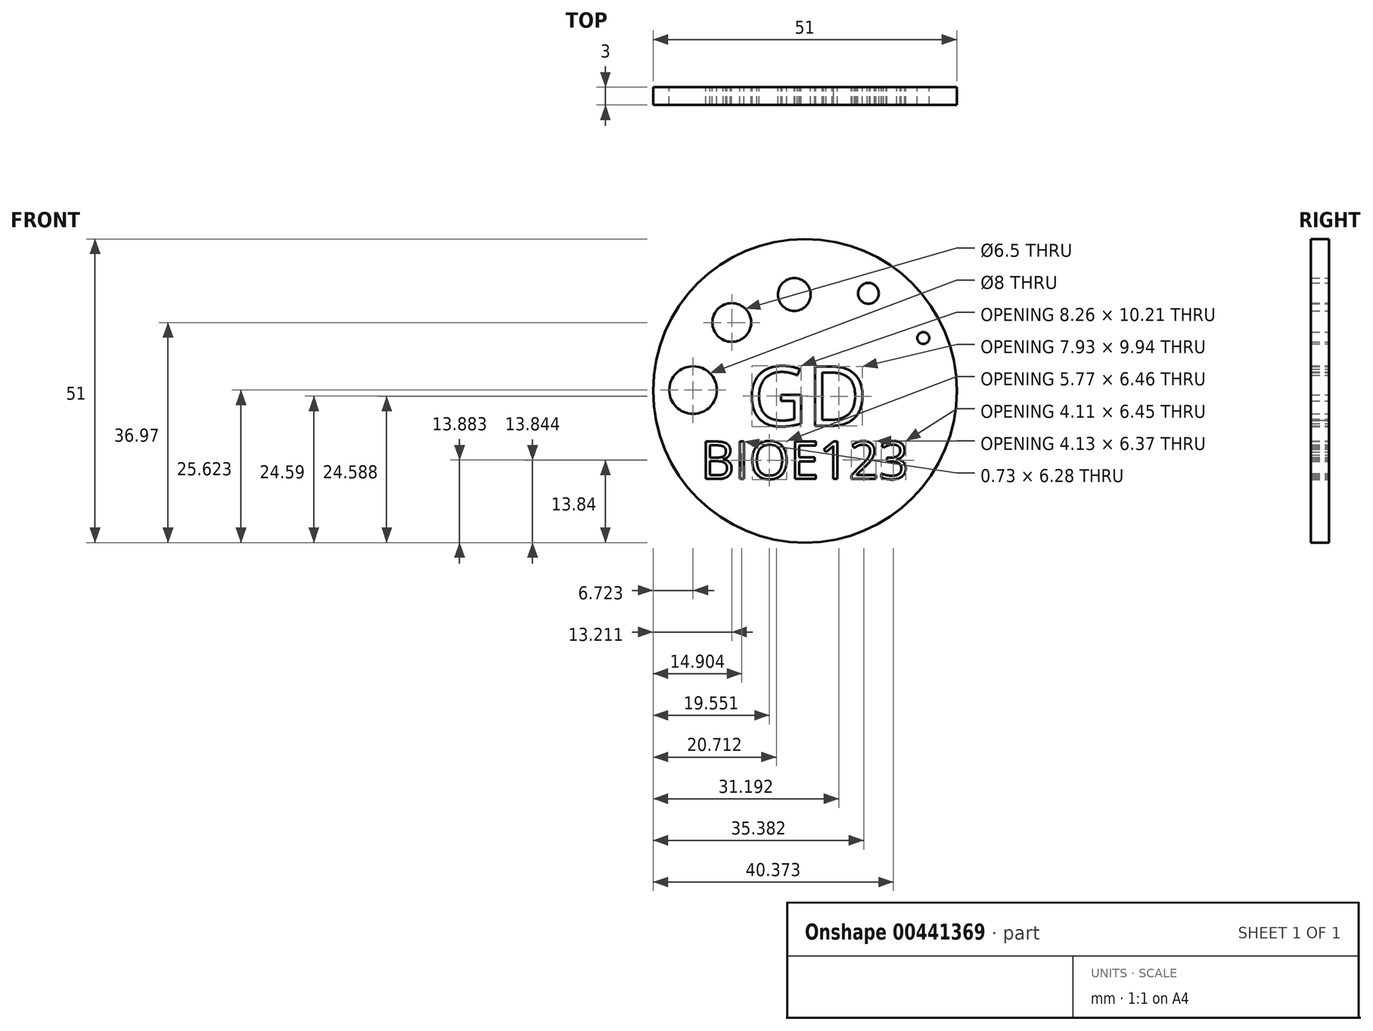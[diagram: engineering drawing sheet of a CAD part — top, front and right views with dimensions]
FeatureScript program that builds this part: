
annotation { "Feature Type Name" : "Feature", "Feature Type Description" : "" }
export const myFeature = defineFeature(function(context is Context, id is Id, definition is map)
    precondition{}
    {
        {
            var Q0;
            Q0=qCreatedBy(makeId("Front.planeOp"),FACE);
            var sketch = newSketch(context, id + "F0", { "sketchPlane" : qUnion([Q0])});
            skCircle(sketch, "E0", {"center": v(0, 0) * mm, "radius": 25.5 * mm});
            skSolve(sketch);
        }
        {
            var Q0;
            Q0 = qSketchRegion(id + "F0", true);
            extrude(context, id + "F1", {"entities" : qUnion([Q0]), "depth" : 3 * mm});
        }
        {
            var Q0;
            Q0=qCreatedBy(makeId("Front.planeOp"),FACE);
            var sketch = newSketch(context, id + "F2", { "sketchPlane" : qUnion([Q0])});
            skCircle(sketch, "E1", {"center": v(-18.78, 0.12) * mm, "radius": 4 * mm});
            skCircle(sketch, "E2", {"center": v(-12.29, 11.47) * mm, "radius": 3.25 * mm});
            skCircle(sketch, "E3", {"center": v(-1.78, 16.17) * mm, "radius": 2.75 * mm});
            skCircle(sketch, "E4", {"center": v(10.66, 16.36) * mm, "radius": 1.75 * mm});
            skCircle(sketch, "E5", {"center": v(19.87, 8.86) * mm, "radius": 1 * mm});
            skSolve(sketch);
        }
        {
            var Q0;
            Q0 = qSketchRegion(id + "F2", true);
            extrude(context, id + "F3", {"entities" : qUnion([Q0]), "operationType" : NewBodyOperationType.REMOVE, "depth" : 3 * mm});
        }
        {
            var Q0;
            Q0=qCreatedBy(makeId("Front.planeOp"),FACE);
            var sketch = newSketch(context, id + "F4", { "sketchPlane" : qUnion([Q0])});
            skText(sketch, "E6", { "text": "BIOE123", "fontName": "OpenSans-Regular.ttf"});
            const initialGuessF4  = {"E6": [-0.01752, -0.0148, 1, 0, 0.00633]};
            skSetInitialGuess(sketch, initialGuessF4);
            skSolve(sketch);
        }
        {
            var Q0;
            Q0 = qSketchRegion(id + "F4", true);
            extrude(context, id + "F5", {"entities" : qUnion([Q0]), "operationType" : NewBodyOperationType.REMOVE, "depth" : 3 * mm});
        }
        {
            var Q0;
            Q0=qCreatedBy(makeId("Front.planeOp"),FACE);
            var sketch = newSketch(context, id + "F6", { "sketchPlane" : qUnion([Q0])});
            skText(sketch, "E7", { "text": "GD", "fontName": "OpenSans-Regular.ttf"});
            const initialGuessF6  = {"E7": [-0.00977, -0.00588, 1, 0, 0.01002]};
            skSetInitialGuess(sketch, initialGuessF6);
            skSolve(sketch);
        }
        {
            var Q0;
            Q0 = qSketchRegion(id + "F6", true);
            extrude(context, id + "F7", {"entities" : qUnion([Q0]), "operationType" : NewBodyOperationType.REMOVE, "depth" : 3 * mm});
        }
    });
